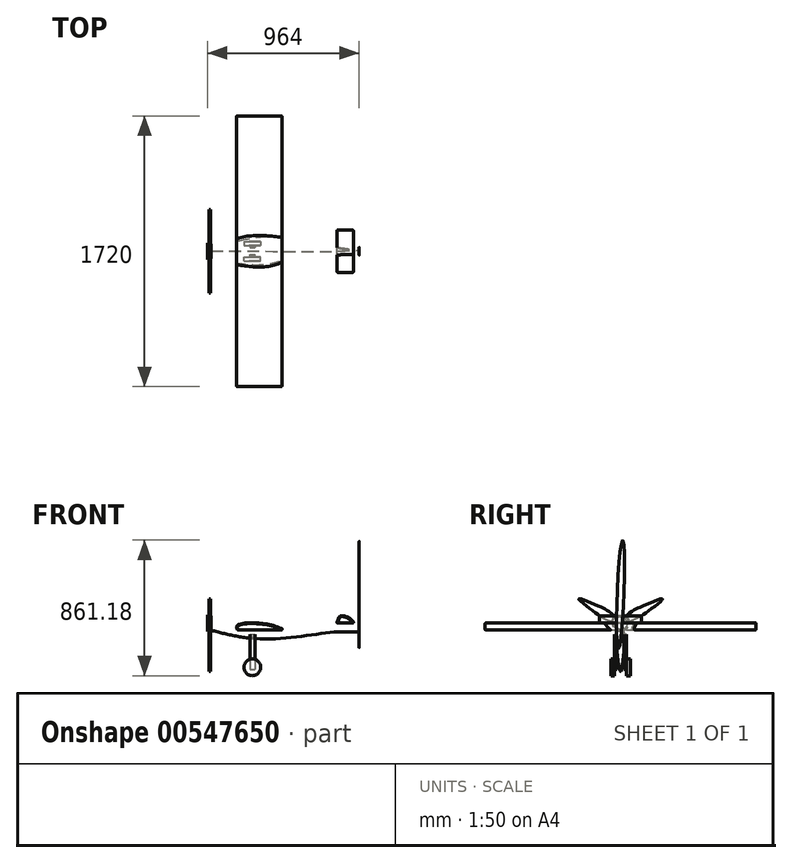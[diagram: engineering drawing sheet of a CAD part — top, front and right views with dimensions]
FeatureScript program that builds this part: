
annotation { "Feature Type Name" : "Feature", "Feature Type Description" : "" }
export const myFeature = defineFeature(function(context is Context, id is Id, definition is map)
    precondition{}
    {
        {
            var Q0;
            Q0=qCreatedBy(makeId("Right.planeOp"),FACE);
            var sketch = newSketch(context, id + "F0", { "sketchPlane" : qUnion([Q0])});
            skCircle(sketch, "E0", {"center": v(0, 0) * mm, "radius": 45 * mm});
            skSolve(sketch);
        }
        {
            var Q0;
            Q0=qCreatedBy(makeId("Right.planeOp"),FACE);
            cPlane(context, id + "F1", {"entities" : qUnion([Q0]), "cplaneType" : CPlaneType.OFFSET, "offset" : 300 * mm, "width" : 150 * mm, "height" : 150 * mm});
        }
        {
            var Q0;
            Q0=qCreatedBy(id+"F1.planeOp",FACE);
            var sketch = newSketch(context, id + "F2", { "sketchPlane" : qUnion([Q0])});
            skCircle(sketch, "E1", {"center": v(0, 0) * mm, "radius": 100 * mm});
            skSolve(sketch);
        }
        {
            var Q0;
            Q0=qCreatedBy(makeId("Right.planeOp"),FACE);
            cPlane(context, id + "F3", {"entities" : qUnion([Q0]), "cplaneType" : CPlaneType.OFFSET, "offset" : 800 * mm, "width" : 150 * mm, "height" : 150 * mm});
        }
        {
            var Q0;
            Q0=qCreatedBy(id+"F3.planeOp",FACE);
            var sketch = newSketch(context, id + "F4", { "sketchPlane" : qUnion([Q0])});
            skEllipse(sketch, "E2", {"center": v(0, 33.36) * mm, "majorRadius": 90 * mm, "minorRadius": 25.19 * mm, "majorAxis": v(0, -1)});
            skSolve(sketch);
        }
        {
            var Q0;
            Q0=qCreatedBy(makeId("Right.planeOp"),FACE);
            cPlane(context, id + "F5", {"entities" : qUnion([Q0]), "cplaneType" : CPlaneType.OFFSET, "offset" : 944 * mm, "width" : 150 * mm, "height" : 150 * mm});
        }
        {
            var Q0;
            Q0=qCreatedBy(id+"F5.planeOp",FACE);
            var sketch = newSketch(context, id + "F6", { "sketchPlane" : qUnion([Q0])});
            skEllipse(sketch, "E3", {"center": v(0, 182.18) * mm, "majorRadius": 345 * mm, "minorRadius": 21.68 * mm, "majorAxis": v(-0.04, -1)});
            skSolve(sketch);
        }
        {
            var Q0;
            Q0=makeQuery(id+"F0.imprint","IMPRINT",FACE,{"disambiguationData":[TD([[makeQuery(id+"F0.imprint","IMPRINT",EDGE,{"derivedFrom":sQuery(id+"F0.wireOp",EDGE,"E0")}),1.0]])]});
            var Q1;
            Q1=makeQuery(id+"F2.imprint","IMPRINT",FACE,{"disambiguationData":[TD([[makeQuery(id+"F2.imprint","IMPRINT",EDGE,{"derivedFrom":sQuery(id+"F2.wireOp",EDGE,"E1")}),1.0]])]});
            var Q2;
            Q2=makeQuery(id+"F4.imprint","IMPRINT",FACE,{"disambiguationData":[TD([[makeQuery(id+"F4.imprint","IMPRINT",EDGE,{"derivedFrom":sQuery(id+"F4.wireOp",EDGE,"E2")}),1.0]])]});
            var Q3;
            Q3=makeQuery(id+"F6.imprint","IMPRINT",FACE,{"disambiguationData":[TD([[makeQuery(id+"F6.imprint","IMPRINT",EDGE,{"derivedFrom":sQuery(id+"F6.wireOp",EDGE,"E3")}),1.0]])]});
            loft(context, id + "F7", {"sheetProfilesArray" : [{ "sheetProfileEntities" : qUnion([Q0]) }, { "sheetProfileEntities" : qUnion([Q1]) }, { "sheetProfileEntities" : qUnion([Q2]) }, { "sheetProfileEntities" : qUnion([Q3]) }]});
        }
        {
            var Q0;
            Q0=qCreatedBy(makeId("Front.planeOp"),FACE);
            var sketch = newSketch(context, id + "F8", { "sketchPlane" : qUnion([Q0])});
            skLineSegment(sketch, "E4", {"start": v(471.8, -45.09) * mm, "end": v(173, -45.09) * mm});
            skFitSpline(sketch, "E5", {"points": [v(471.8, -45.09) * mm, v(308.92, 0) * mm, v(173, -45.09) * mm], "startDerivative": vector(-198.46, 99.66) * mm, "endDerivative": vector(243.71, -282.22) * mm});
            skSolve(sketch);
        }
        {
            var Q0;
            Q0=makeQuery(id+"F8.imprint","IMPRINT",FACE,{"disambiguationData":[TD([[makeQuery(id+"F8.imprint","IMPRINT",EDGE,{"derivedFrom":sQuery(id+"F8.wireOp",EDGE,"E4")}),-1.0]])]});
            extrude(context, id + "F9", {"entities" : qUnion([Q0]), "endBound" : BoundingType.SYMMETRIC, "oppositeDirection" : true, "depth" : 1720 * mm, "offsetDistance" : 25 * mm});
        }
        {
            var Q0;
            Q0=makeQuery(id+"F9.opExtrude","CAP_EDGE",EDGE,{"disambiguationData":[OSD([sQuery(id+"F8.wireOp",EDGE,"E5")])],"isStart":false});
            var Q1;
            Q1=makeQuery(id+"F9.opExtrude","CAP_EDGE",EDGE,{"disambiguationData":[OSD([sQuery(id+"F8.wireOp",EDGE,"E4")])],"isStart":false});
            var Q2;
            {var subQ0=sQuery(id+"F8.wireOp",EDGE,"E5");var subQ1=sQuery(id+"F8.wireOp",EDGE,"E4");Q2=makeQuery(id+"F9.opExtrude","SWEPT_EDGE",EDGE,{"disambiguationData":[OSD([subQ1,subQ0]),TDD([makeQuery(id+"F8.imprint","INTERSECT",VERTEX,{"disambiguationData":[OD(0.0)],"derivedFrom":[subQ1,subQ0]})])]});}
            var Q3;
            {var subQ0=sQuery(id+"F8.wireOp",EDGE,"E5");var subQ1=sQuery(id+"F8.wireOp",EDGE,"E4");Q3=makeQuery(id+"F9.opExtrude","SWEPT_EDGE",EDGE,{"disambiguationData":[OSD([subQ1,subQ0]),TDD([makeQuery(id+"F8.imprint","INTERSECT",VERTEX,{"disambiguationData":[OD(1.0)],"derivedFrom":[subQ1,subQ0]})])]});}
            var Q4;
            Q4=makeQuery(id+"F9.opExtrude","CAP_EDGE",EDGE,{"disambiguationData":[OSD([sQuery(id+"F8.wireOp",EDGE,"E5")])],"isStart":true});
            var Q5;
            Q5=makeQuery(id+"F9.opExtrude","CAP_EDGE",EDGE,{"disambiguationData":[OSD([sQuery(id+"F8.wireOp",EDGE,"E4")])],"isStart":true});
            fillet(context, id + "F10", {"entities" : qUnion([Q0, Q1, Q2, Q3, Q4, Q5]), "radius" : 5 * mm, "tangentPropagation" : true, "allowEdgeOverflow" : false});
        }
        {
            var Q0;
            Q0=makeQuery(id+"F7.opLoft","MID_CAP_EDGE",EDGE,{"disambiguationData":[OSD([sQuery(id+"F0.wireOp",EDGE,"E0")])],"capPos":0.0});
            fillet(context, id + "F11", {"entities" : qUnion([Q0]), "radius" : 5 * mm, "tangentPropagation" : true, "allowEdgeOverflow" : false});
        }
        {
            var Q0;
            Q0=qCreatedBy(makeId("Right.planeOp"),FACE);
            var sketch = newSketch(context, id + "F12", { "sketchPlane" : qUnion([Q0])});
            skFitSpline(sketch, "E6", {"points": [v(19.63, -48.7) * mm, v(24.13, -165) * mm, v(0, -307.12) * mm, v(-24.59, -168.38) * mm, v(-19.81, -48.62) * mm], "startDerivative": vector(189.95, -853.35) * mm, "endDerivative": vector(104.14, 846.7) * mm});
            skFitSpline(sketch, "E7", {"points": [v(19.63, -48.7) * mm, v(0, -54.81) * mm, v(-19.81, -48.62) * mm], "startDerivative": vector(-39.31, -22.1) * mm, "endDerivative": vector(-39.58, 22.22) * mm});
            skSolve(sketch);
        }
        {
            var Q0;
            Q0=qCreatedBy(makeId("Right.planeOp"),FACE);
            var sketch = newSketch(context, id + "F13", { "sketchPlane" : qUnion([Q0])});
            skCircle(sketch, "E8", {"center": v(0, 0) * mm, "radius": 52.5 * mm});
            skSolve(sketch);
        }
        {
            var Q0;
            Q0=makeQuery(id+"F12.imprint","IMPRINT",FACE,{"disambiguationData":[TD([[makeQuery(id+"F12.imprint","IMPRINT",EDGE,{"derivedFrom":sQuery(id+"F12.wireOp",EDGE,"E6")}),-1.0]])]});
            extrude(context, id + "F14", {"entities" : qUnion([Q0]), "oppositeDirection" : true, "depth" : 10 * mm, "offsetDistance" : 25 * mm});
        }
        {
            var Q0;
            Q0=makeQuery(id+"F13.imprint","IMPRINT",FACE,{"disambiguationData":[TD([[makeQuery(id+"F13.imprint","IMPRINT",EDGE,{"derivedFrom":sQuery(id+"F13.wireOp",EDGE,"E8")}),1.0]])]});
            extrude(context, id + "F15", {"entities" : qUnion([Q0]), "oppositeDirection" : true, "depth" : 20 * mm, "offsetDistance" : 25 * mm});
        }
        {
            var Q0;
            Q0=makeQuery(id+"F14.opExtrude","SWEPT_BODY",BODY,{"disambiguationData":[OSD([sQuery(id+"F12.wireOp",EDGE,"E6"),sQuery(id+"F12.wireOp",EDGE,"E7")])]});
            var Q1;
            Q1=makeQuery(id+"F15.opExtrude","CAP_EDGE",EDGE,{"disambiguationData":[OSD([sQuery(id+"F13.wireOp",EDGE,"E8")])],"isStart":false});
            circularPattern(context, id + "F16", {"entities" : qUnion([Q0]), "axis" : qUnion([Q1]), "angle" : 360 * degree, "instanceCount" : 3, "equalSpace" : true});
        }
        {
            var Q0;
            Q0=qCreatedBy(makeId("Front.planeOp"),FACE);
            var sketch = newSketch(context, id + "F17", { "sketchPlane" : qUnion([Q0])});
            skLineSegment(sketch, "E9", {"start": v(799.24, 0) * mm, "end": v(910.62, 0) * mm});
            skFitSpline(sketch, "E10", {"points": [v(799.24, 0) * mm, v(818.78, 41.04) * mm, v(855.9, 43) * mm, v(910.62, 0) * mm], "startDerivative": vector(89.5, 138.42) * mm, "endDerivative": vector(78.73, -169.48) * mm});
            skSolve(sketch);
        }
        {
            var Q0;
            Q0=makeQuery(id+"F17.imprint","IMPRINT",FACE,{"disambiguationData":[TD([[makeQuery(id+"F17.imprint","IMPRINT",EDGE,{"derivedFrom":sQuery(id+"F17.wireOp",EDGE,"E9")}),1.0]])]});
            extrude(context, id + "F18", {"entities" : qUnion([Q0]), "endBound" : BoundingType.SYMMETRIC, "depth" : 268 * mm, "offsetDistance" : 25 * mm});
        }
        {
            var Q0;
            Q0=makeQuery(id+"F18.opExtrude","CAP_FACE",FACE,{"disambiguationData":[OSD([sQuery(id+"F17.wireOp",EDGE,"E9"),sQuery(id+"F17.wireOp",EDGE,"E10")])],"isStart":false});
            var Q1;
            {var subQ0=sQuery(id+"F17.wireOp",EDGE,"E10");var subQ1=sQuery(id+"F17.wireOp",EDGE,"E9");Q1=makeQuery(id+"F18.opExtrude","SWEPT_EDGE",EDGE,{"disambiguationData":[OSD([subQ1,subQ0]),TDD([makeQuery(id+"F17.imprint","INTERSECT",VERTEX,{"disambiguationData":[OD(1.0)],"derivedFrom":[subQ1,subQ0]})])]});}
            var Q2;
            Q2=makeQuery(id+"F18.opExtrude","CAP_EDGE",EDGE,{"disambiguationData":[OSD([sQuery(id+"F17.wireOp",EDGE,"E10")])],"isStart":true});
            var Q3;
            Q3=makeQuery(id+"F18.opExtrude","CAP_EDGE",EDGE,{"disambiguationData":[OSD([sQuery(id+"F17.wireOp",EDGE,"E9")])],"isStart":true});
            var Q4;
            Q4=makeQuery(id+"F18.opExtrude","SWEPT_FACE",FACE,{"disambiguationData":[OSD([sQuery(id+"F17.wireOp",EDGE,"E10")])]});
            var Q5;
            {var subQ0=sQuery(id+"F17.wireOp",EDGE,"E10");var subQ1=sQuery(id+"F17.wireOp",EDGE,"E9");Q5=makeQuery(id+"F18.opExtrude","SWEPT_EDGE",EDGE,{"disambiguationData":[OSD([subQ1,subQ0]),TDD([makeQuery(id+"F17.imprint","INTERSECT",VERTEX,{"disambiguationData":[OD(0.0)],"derivedFrom":[subQ1,subQ0]})])]});}
            fillet(context, id + "F19", {"entities" : qUnion([Q0, Q1, Q2, Q3, Q4, Q5]), "radius" : 5 * mm, "tangentPropagation" : true, "allowEdgeOverflow" : false});
        }
        {
            var Q0;
            Q0=qCreatedBy(makeId("Front.planeOp"),FACE);
            cPlane(context, id + "F20", {"entities" : qUnion([Q0]), "cplaneType" : CPlaneType.OFFSET, "offset" : 30 * mm, "width" : 150 * mm, "height" : 150 * mm});
        }
        {
            var Q0;
            Q0=qCreatedBy(id+"F20.planeOp",FACE);
            var sketch = newSketch(context, id + "F21", { "sketchPlane" : qUnion([Q0])});
            skLineSegment(sketch, "E11.bottom", {"start": v(248.94, -70.58) * mm, "end": v(280.81, -70.58) * mm});
            skLineSegment(sketch, "E11.top", {"start": v(248.94, -294.75) * mm, "end": v(280.81, -294.75) * mm});
            skLineSegment(sketch, "E11.left", {"start": v(248.94, -70.58) * mm, "end": v(248.94, -294.75) * mm});
            skLineSegment(sketch, "E11.right", {"start": v(280.81, -70.58) * mm, "end": v(280.81, -294.75) * mm});
            skSolve(sketch);
        }
        {
            var Q0;
            Q0=makeQuery(id+"F21.imprint","IMPRINT",FACE,{"disambiguationData":[TD([[makeQuery(id+"F21.imprint","IMPRINT",EDGE,{"derivedFrom":sQuery(id+"F21.wireOp",EDGE,"E11.bottom")}),-1.0]])]});
            extrude(context, id + "F22", {"entities" : qUnion([Q0]), "endBound" : BoundingType.SYMMETRIC, "depth" : 15 * mm, "offsetDistance" : 25 * mm});
        }
        {
            var Q0;
            Q0=makeQuery(id+"F22.opExtrude","CAP_FACE",FACE,{"disambiguationData":[OSD([sQuery(id+"F21.wireOp",EDGE,"E11.bottom"),sQuery(id+"F21.wireOp",EDGE,"E11.top"),sQuery(id+"F21.wireOp",EDGE,"E11.left"),sQuery(id+"F21.wireOp",EDGE,"E11.right")])],"isStart":false});
            var sketch = newSketch(context, id + "F23", { "sketchPlane" : qUnion([Q0])});
            skCircle(sketch, "E12", {"center": v(264.87, -281.08) * mm, "radius": 53.17 * mm});
            skPoint(sketch, "E12.centerSnap0", {"position": v(264.87, -294.75) * mm});
            skSolve(sketch);
        }
        {
            var Q0;
            {var subQ5=makeQuery(id+"F22.opExtrude","CAP_EDGE",EDGE,{"disambiguationData":[OSD([sQuery(id+"F21.wireOp",EDGE,"E11.top")])],"isStart":false});Q0=makeQuery(id+"F23.imprint","IMPRINT",FACE,{"disambiguationData":[TD([[makeQuery(id+"F23.imprint","IMPRINT",EDGE,{"derivedFrom":subQ5}),1.0]])]});}
            var Q1;
            {var subQ5=makeQuery(id+"F22.opExtrude","CAP_EDGE",EDGE,{"disambiguationData":[OSD([sQuery(id+"F21.wireOp",EDGE,"E11.top")])],"isStart":false});Q1=makeQuery(id+"F23.imprint","IMPRINT",FACE,{"disambiguationData":[TD([[makeQuery(id+"F23.imprint","IMPRINT",EDGE,{"derivedFrom":subQ5}),-1.0]])]});}
            extrude(context, id + "F24", {"entities" : qUnion([Q0, Q1]), "depth" : 25 * mm, "offsetDistance" : 25 * mm});
        }
        {
            var Q0;
            Q0=makeQuery(id+"F22.opExtrude","SWEPT_BODY",BODY,{"disambiguationData":[OSD([sQuery(id+"F21.wireOp",EDGE,"E11.bottom"),sQuery(id+"F21.wireOp",EDGE,"E11.top"),sQuery(id+"F21.wireOp",EDGE,"E11.left"),sQuery(id+"F21.wireOp",EDGE,"E11.right")])]});
            var Q1;
            Q1=makeQuery(id+"F24.opExtrude","SWEPT_BODY",BODY,{"disambiguationData":[OSD([sQuery(id+"F23.wireOp",EDGE,"E12")])]});
            var Q2;
            Q2=qCreatedBy(makeId("Front.planeOp"),FACE);
            mirror(context, id + "F25", {"entities" : qUnion([Q0, Q1]), "mirrorPlane" : qUnion([Q2])});
        }
        {
            var Q0;
            Q0=makeQuery(id+"F24.opExtrude","SWEPT_BODY",BODY,{"disambiguationData":[OSD([sQuery(id+"F23.wireOp",EDGE,"E12")])]});
            var Q1;
            Q1=makeQuery(id+"F25.opPattern","COPY",BODY,{"derivedFrom":makeQuery(id+"F22.opExtrude","SWEPT_BODY",BODY,{"disambiguationData":[OSD([sQuery(id+"F21.wireOp",EDGE,"E11.bottom"),sQuery(id+"F21.wireOp",EDGE,"E11.top"),sQuery(id+"F21.wireOp",EDGE,"E11.left"),sQuery(id+"F21.wireOp",EDGE,"E11.right")])]}),"instanceName":"1"});
            var Q2;
            Q2=makeQuery(id+"F7.opLoft","SWEPT_BODY",BODY,{"disambiguationData":[OSD([makeQuery(id+"F0.imprint","IMPRINT",FACE,{"disambiguationData":[TD([[makeQuery(id+"F0.imprint","IMPRINT",EDGE,{"derivedFrom":sQuery(id+"F0.wireOp",EDGE,"E0")}),1.0]])]}),sQuery(id+"F2.wireOp",EDGE,"E1"),sQuery(id+"F4.wireOp",EDGE,"E2"),makeQuery(id+"F6.imprint","IMPRINT",FACE,{"disambiguationData":[TD([[makeQuery(id+"F6.imprint","IMPRINT",EDGE,{"derivedFrom":sQuery(id+"F6.wireOp",EDGE,"E3")}),1.0]])]})])]});
            booleanBodies(context, id + "F26", {"operationType" : BooleanOperationType.SUBTRACTION, "tools" : qUnion([Q0, Q1]), "targets" : qUnion([Q2]), "keepTools" : true});
        }
        {
            var Q0;
            Q0=makeQuery(id+"F9.opExtrude","SWEPT_BODY",BODY,{"disambiguationData":[OSD([sQuery(id+"F8.wireOp",EDGE,"E4"),sQuery(id+"F8.wireOp",EDGE,"E5")])]});
            var Q1;
            Q1=makeQuery(id+"F7.opLoft","SWEPT_BODY",BODY,{"disambiguationData":[OSD([makeQuery(id+"F0.imprint","IMPRINT",FACE,{"disambiguationData":[TD([[makeQuery(id+"F0.imprint","IMPRINT",EDGE,{"derivedFrom":sQuery(id+"F0.wireOp",EDGE,"E0")}),1.0]])]}),sQuery(id+"F2.wireOp",EDGE,"E1"),sQuery(id+"F4.wireOp",EDGE,"E2"),makeQuery(id+"F6.imprint","IMPRINT",FACE,{"disambiguationData":[TD([[makeQuery(id+"F6.imprint","IMPRINT",EDGE,{"derivedFrom":sQuery(id+"F6.wireOp",EDGE,"E3")}),1.0]])]})])]});
            booleanBodies(context, id + "F27", {"operationType" : BooleanOperationType.SUBTRACTION, "tools" : qUnion([Q0]), "targets" : qUnion([Q1]), "keepTools" : true});
        }
        {
            var Q0;
            Q0=makeQuery(id+"F18.opExtrude","SWEPT_BODY",BODY,{"disambiguationData":[OSD([sQuery(id+"F17.wireOp",EDGE,"E9"),sQuery(id+"F17.wireOp",EDGE,"E10")])]});
            var Q1;
            Q1=makeQuery(id+"F7.opLoft","SWEPT_BODY",BODY,{"disambiguationData":[OSD([makeQuery(id+"F0.imprint","IMPRINT",FACE,{"disambiguationData":[TD([[makeQuery(id+"F0.imprint","IMPRINT",EDGE,{"derivedFrom":sQuery(id+"F0.wireOp",EDGE,"E0")}),1.0]])]}),sQuery(id+"F2.wireOp",EDGE,"E1"),sQuery(id+"F4.wireOp",EDGE,"E2"),makeQuery(id+"F6.imprint","IMPRINT",FACE,{"disambiguationData":[TD([[makeQuery(id+"F6.imprint","IMPRINT",EDGE,{"derivedFrom":sQuery(id+"F6.wireOp",EDGE,"E3")}),1.0]])]})])]});
            booleanBodies(context, id + "F28", {"operationType" : BooleanOperationType.SUBTRACTION, "tools" : qUnion([Q0]), "targets" : qUnion([Q1]), "keepTools" : true});
        }
    });
